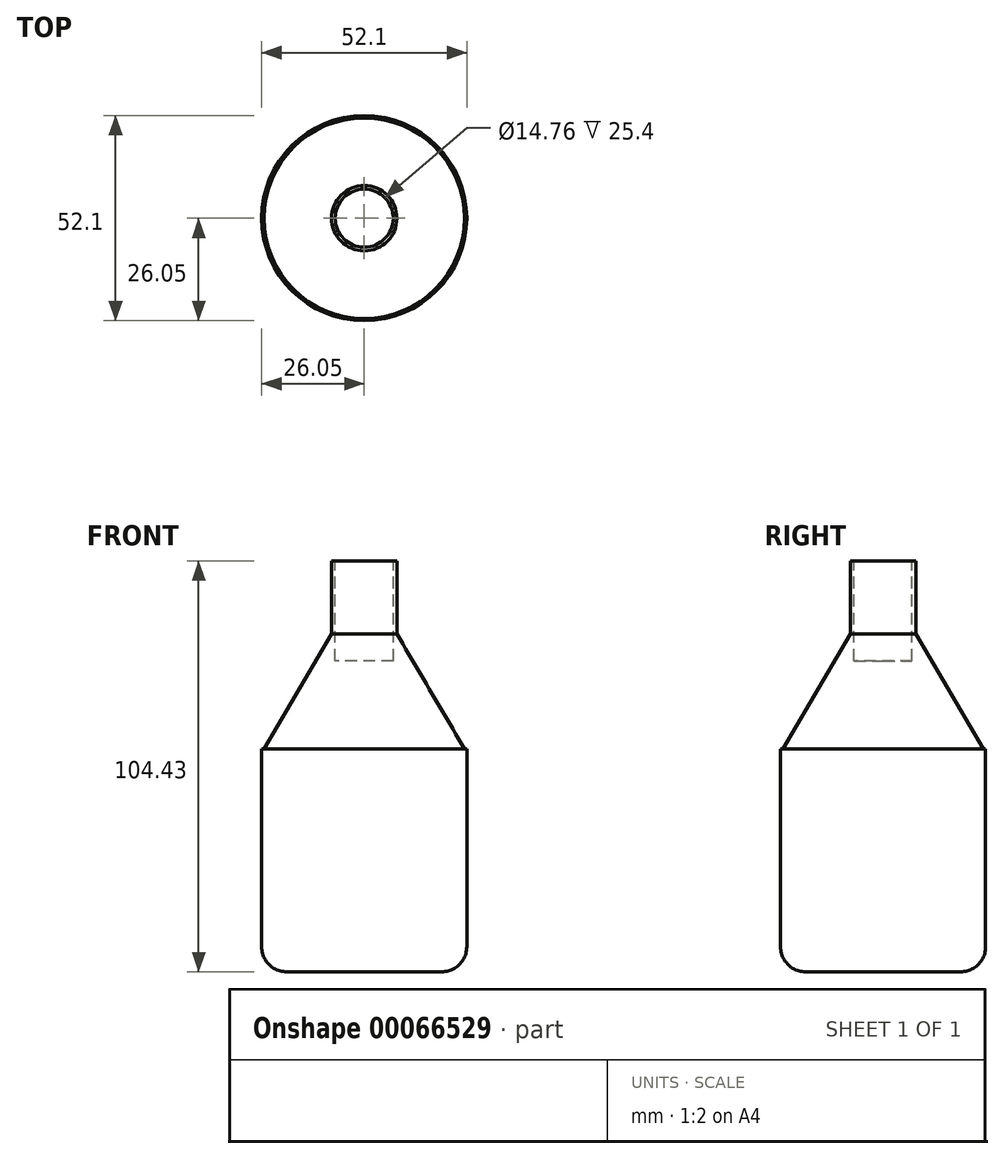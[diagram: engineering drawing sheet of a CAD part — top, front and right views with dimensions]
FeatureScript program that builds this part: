
annotation { "Feature Type Name" : "Feature", "Feature Type Description" : "" }
export const myFeature = defineFeature(function(context is Context, id is Id, definition is map)
    precondition{}
    {
        {
            var Q0;
            Q0=qCreatedBy(makeId("Front.planeOp"),FACE);
            var sketch = newSketch(context, id + "F0", { "sketchPlane" : qUnion([Q0])});
            skLineSegment(sketch, "E0.bottom", {"start": v(0, 0) * mm, "end": v(26.05, 0) * mm});
            skLineSegment(sketch, "E0.top", {"start": v(0, -56.6) * mm, "end": v(19.7, -56.6) * mm});
            skLineSegment(sketch, "E0.left", {"start": v(0, 0) * mm, "end": v(0, -56.6) * mm});
            skLineSegment(sketch, "E0.right", {"start": v(26.05, 0) * mm, "end": v(26.05, -50.25) * mm});
            skPoint(sketch, "E1.visualSharp", {"position": v(26.05, -56.6) * mm});
            skArc(sketch, "E1.filletArc", {"start": v(19.7, -56.6) * mm, "mid": v(24.19, -54.74) * mm, "end": v(26.05, -50.25) * mm});
            skSolve(sketch);
        }
        {
            var Q0;
            Q0=makeQuery(id+"F0.imprint","IMPRINT",FACE,{"disambiguationData":[TD([[makeQuery(id+"F0.imprint","IMPRINT",EDGE,{"derivedFrom":sQuery(id+"F0.wireOp",EDGE,"E0.bottom")}),-1.0]])]});
            var sketch = newSketch(context, id + "F1", { "sketchPlane" : qUnion([Q0])});
            skLineSegment(sketch, "E2", {"start": v(25.48, 0) * mm, "end": v(8.3, 29.3) * mm});
            skLineSegment(sketch, "E3", {"start": v(8.3, 29.3) * mm, "end": v(8.3, 47.83) * mm});
            skLineSegment(sketch, "E4", {"start": v(8.3, 47.83) * mm, "end": v(0, 47.83) * mm});
            skLineSegment(sketch, "E5", {"start": v(0, 47.83) * mm, "end": v(0, 0) * mm});
            skSolve(sketch);
        }
        {
            var Q0;
            Q0=makeQuery(id+"F0.imprint","IMPRINT",FACE,{"disambiguationData":[TD([[makeQuery(id+"F0.imprint","IMPRINT",EDGE,{"derivedFrom":sQuery(id+"F0.wireOp",EDGE,"E0.bottom")}),-1.0]])]});
            var Q1;
            {var subQ1=sQuery(id+"F1.wireOp",EDGE,"E2");Q1=makeQuery(id+"F1.imprint","IMPRINT",FACE,{"disambiguationData":[TD([[makeQuery(id+"F1.imprint","IMPRINT",EDGE,{"derivedFrom":subQ1}),1.0]])]});}
            var Q2;
            Q2=sQuery(id+"F0.wireOp",EDGE,"E0.left");
            revolve(context, id + "F2", {"entities" : qUnion([Q0, Q1]), "axis" : qUnion([Q2]), "revolveType" : RevolveType.FULL});
        }
        {
            var Q0;
            Q0=makeQuery(id+"F2.opRevolve","SWEPT_FACE",FACE,{"disambiguationData":[OSD([sQuery(id+"F1.wireOp",EDGE,"E4")])]});
            var sketch = newSketch(context, id + "F3", { "sketchPlane" : qUnion([Q0])});
            skCircle(sketch, "E6", {"center": v(0, 0) * mm, "radius": 7.38 * mm});
            skSolve(sketch);
        }
        {
            var Q0;
            Q0 = qSketchRegion(id + "F3", true);
            extrude(context, id + "F4", {"entities" : qUnion([Q0]), "operationType" : NewBodyOperationType.REMOVE, "oppositeDirection" : true, "depth" : 25.4 * mm});
        }
    });
